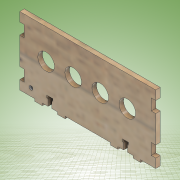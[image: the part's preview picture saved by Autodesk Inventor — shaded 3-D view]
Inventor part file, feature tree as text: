
AUTODESK INVENTOR PART (.ipt)
format: ipt  version: 2022 (Build 260153000, 153)  size: 251,392 bytes
history: native  units: mm
features: extrude x4, sketch x4, other x1
ambient origin geometry x8: Origin, YZ Plane, XZ Plane, XY Plane, X Axis, Y Axis, Z Axis, Center Point
bodies: Body1 (feature_tree)
feature tree (9):
  other  "Sólido1"
  extrude  "Extrusión1"  Depth=90.0mm
  sketch  "Boceto4"  dims[d4=50.0mm d6=35.8mm]
  sketch  "Boceto5"  dims[d7=35.8mm d8=35.8mm]
  extrude  "Extrusión2"  Depth=50.0mm
  extrude  "Extrusión3"  Depth=35.8mm
  extrude  "Extrusión5"  Depth=6.0mm TaperAngle=0.0deg
  sketch  "Boceto3"  dims[d1=90.0mm d3=22.0mm]
  sketch  "Boceto7"  dims[d9=35.0mm d10=6.0mm d11=0.0mm d12=8.0mm d13=3.1mm d14=5.0mm d15=12.0mm d16=40.0mm d17=10.0mm d18=10.0mm d19=20.0mm d20=20.0mm d21=0.0mm d22=0.0mm d23=3.0mm d24=0.0mm d31=6.0mm d32=15.0mm d33=12.0mm d34=0.0mm d35=0.0mm d37=5.0mm d38=10.0mm d39=15.0mm d40=180.0mm]
